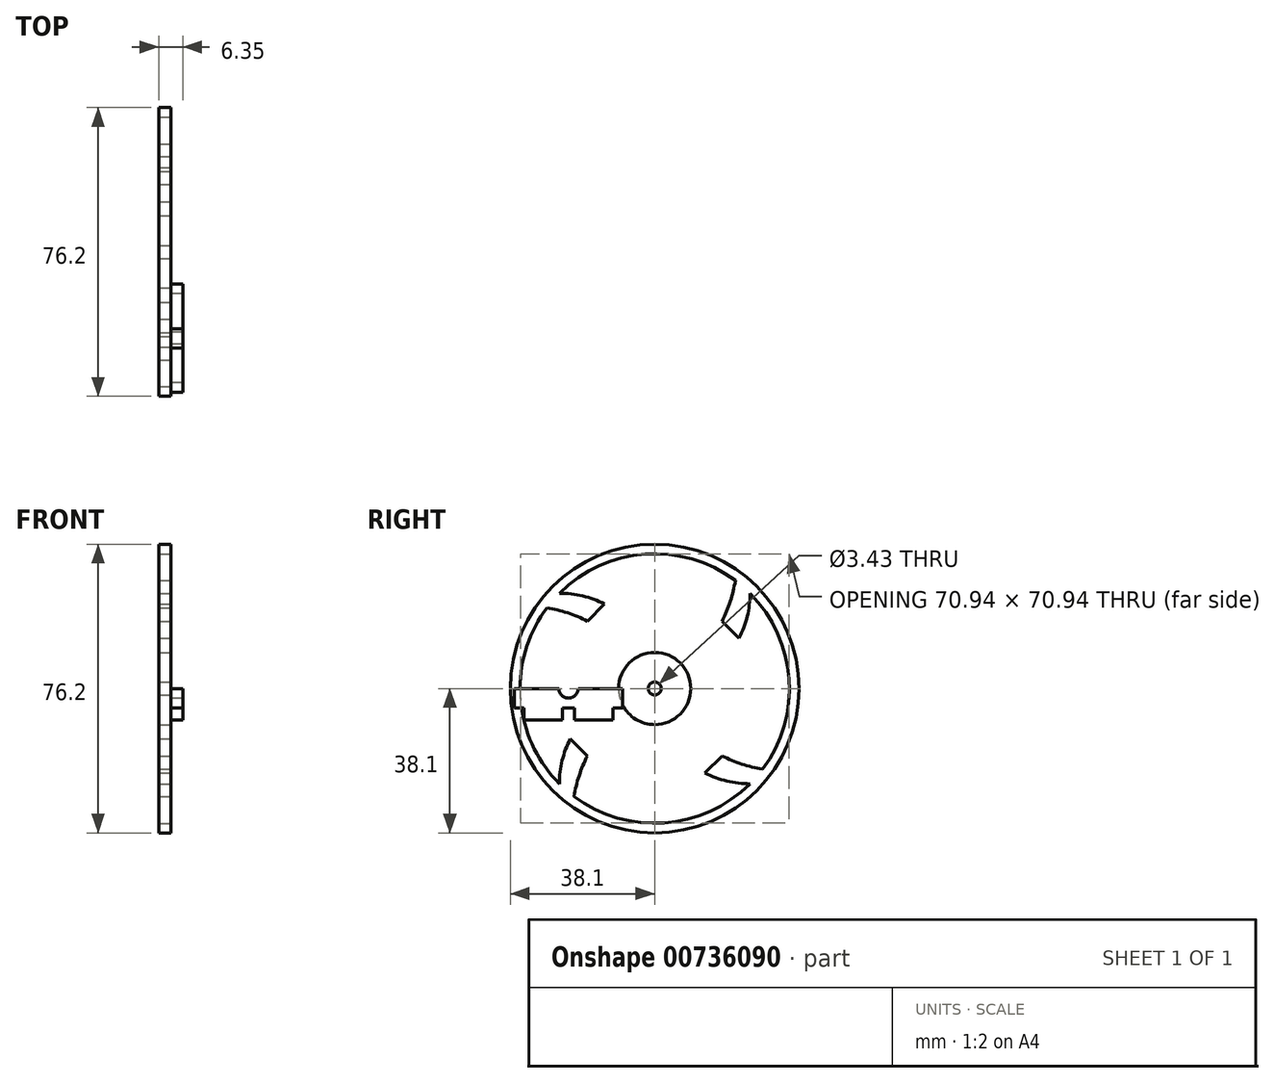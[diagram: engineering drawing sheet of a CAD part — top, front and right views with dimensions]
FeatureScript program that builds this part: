
annotation { "Feature Type Name" : "Feature", "Feature Type Description" : "" }
export const myFeature = defineFeature(function(context is Context, id is Id, definition is map)
    precondition{}
    {
        {
            var Q0;
            Q0=qCreatedBy(makeId("Right.planeOp"),FACE);
            var sketch = newSketch(context, id + "F0", { "sketchPlane" : qUnion([Q0])});
            skLineSegment(sketch, "E0.bottom", {"start": v(-34.5, -5.08) * mm, "end": v(-24.35, -5.08) * mm});
            skLineSegment(sketch, "E0.top", {"start": v(-34.5, -8.25) * mm, "end": v(-24.35, -8.25) * mm});
            skLineSegment(sketch, "E0.left", {"start": v(-34.5, -5.08) * mm, "end": v(-34.5, -8.25) * mm});
            skLineSegment(sketch, "E0.right", {"start": v(-24.35, -5.08) * mm, "end": v(-24.35, -8.25) * mm});
            skLineSegment(sketch, "E1", {"start": v(-24.35, -5.08) * mm, "end": v(-21.17, -5.08) * mm});
            skLineSegment(sketch, "E2.bottom", {"start": v(-21.17, -5.08) * mm, "end": v(-11.01, -5.08) * mm});
            skLineSegment(sketch, "E2.top", {"start": v(-21.17, -8.25) * mm, "end": v(-11.01, -8.25) * mm});
            skLineSegment(sketch, "E2.left", {"start": v(-21.17, -5.08) * mm, "end": v(-21.17, -8.25) * mm});
            skLineSegment(sketch, "E2.right", {"start": v(-11.01, -5.08) * mm, "end": v(-11.01, -8.25) * mm});
            skLineSegment(sketch, "E3", {"start": v(-11.01, -5.08) * mm, "end": v(-8.47, -5.08) * mm});
            skLineSegment(sketch, "E4", {"start": v(-8.47, -5.08) * mm, "end": v(-8.47, 0) * mm});
            skLineSegment(sketch, "E5", {"start": v(-34.5, -5.08) * mm, "end": v(-37.05, -5.08) * mm});
            skLineSegment(sketch, "E6", {"start": v(-37.05, -5.08) * mm, "end": v(-37.05, 0) * mm});
            skLineSegment(sketch, "E7", {"start": v(-37.05, 0) * mm, "end": v(-8.47, 0) * mm});
            skCircle(sketch, "E8", {"center": v(-22.76, 0) * mm, "radius": 1.59 * mm});
            skCircle(sketch, "E9", {"center": v(-22.76, 0) * mm, "radius": 2.54 * mm});
            skSolve(sketch);
        }
        {
            var Q0;
            Q0=makeQuery(id+"F0.imprint","IMPRINT",FACE,{"disambiguationData":[TD([[makeQuery(id+"F0.imprint","IMPRINT",EDGE,{"derivedFrom":sQuery(id+"F0.wireOp",EDGE,"E0.bottom")}),1.0]])]});
            var Q1;
            Q1=makeQuery(id+"F0.imprint","IMPRINT",FACE,{"disambiguationData":[TD([[makeQuery(id+"F0.imprint","IMPRINT",EDGE,{"derivedFrom":sQuery(id+"F0.wireOp",EDGE,"E0.bottom")}),-1.0]])]});
            var Q2;
            Q2=makeQuery(id+"F0.imprint","IMPRINT",FACE,{"disambiguationData":[TD([[makeQuery(id+"F0.imprint","IMPRINT",EDGE,{"derivedFrom":sQuery(id+"F0.wireOp",EDGE,"E2.bottom")}),-1.0]])]});
            var Q3;
            {var subQ0=sQuery(id+"F0.wireOp",EDGE,"E9");var subQ1=sQuery(id+"F0.wireOp",EDGE,"E7");var subQ2=makeQuery(id+"F0.imprint","INTERSECT",VERTEX,{"disambiguationData":[OD(0.0)],"derivedFrom":[subQ1,subQ0]});Q3=makeQuery(id+"F0.imprint","IMPRINT",FACE,{"disambiguationData":[TD([[makeQuery(id+"F0.imprint","IMPRINT",EDGE,{"disambiguationData":[TD([[subQ2,-1.0]])],"derivedFrom":subQ1}),-1.0]])]});}
            var Q4;
            {var subQ0=sQuery(id+"F0.wireOp",EDGE,"E9");var subQ1=sQuery(id+"F0.wireOp",EDGE,"E7");var subQ2=makeQuery(id+"F0.imprint","INTERSECT",VERTEX,{"disambiguationData":[OD(0.0)],"derivedFrom":[subQ1,subQ0]});Q4=makeQuery(id+"F0.imprint","IMPRINT",FACE,{"disambiguationData":[TD([[makeQuery(id+"F0.imprint","IMPRINT",EDGE,{"disambiguationData":[TD([[subQ2,-1.0]])],"derivedFrom":subQ1}),1.0]])]});}
            extrude(context, id + "F1", {"entities" : qUnion([Q0, Q1, Q2, Q3, Q4]), "depth" : 3.17 * mm, "offsetDistance" : 25.4 * mm});
        }
        {
            var Q0;
            Q0=qCreatedBy(makeId("Right.planeOp"),FACE);
            var sketch = newSketch(context, id + "F2", { "sketchPlane" : qUnion([Q0])});
            skCircle(sketch, "E10", {"center": v(0, 0) * mm, "radius": 1.71 * mm});
            skCircle(sketch, "E11", {"center": v(0, 0) * mm, "radius": 38.1 * mm});
            skCircle(sketch, "E12", {"center": v(0, 0) * mm, "radius": 35.56 * mm});
            skLineSegment(sketch, "E13", {"start": v(0, 35.56) * mm, "end": v(-35.56, 0) * mm});
            skLineSegment(sketch, "E14", {"start": v(-35.56, 0) * mm, "end": v(0, -35.56) * mm});
            skLineSegment(sketch, "E15", {"start": v(0, -35.56) * mm, "end": v(35.56, 0) * mm});
            skLineSegment(sketch, "E16", {"start": v(35.56, 0) * mm, "end": v(0, 35.56) * mm});
            skLineSegment(sketch, "E17", {"start": v(-17.78, 17.78) * mm, "end": v(-25.14, 25.14) * mm});
            skLineSegment(sketch, "E18", {"start": v(0, 0) * mm, "end": v(-1.21, -1.21) * mm});
            skLineSegment(sketch, "E19", {"start": v(0, 0) * mm, "end": v(-1.71, 0) * mm});
            skLineSegment(sketch, "E20", {"start": v(0, 0) * mm, "end": v(-1.21, 1.21) * mm});
            skLineSegment(sketch, "E21.MirrorCS", {"start": v(17.78, -17.78) * mm, "end": v(25.14, -25.14) * mm});
            skLineSegment(sketch, "E22", {"start": v(17.78, 17.78) * mm, "end": v(25.14, 25.14) * mm});
            skLineSegment(sketch, "E23.MirrorCS", {"start": v(-17.78, -17.78) * mm, "end": v(-25.14, -25.14) * mm});
            skLineSegment(sketch, "E24.MirrorCS", {"start": v(0, 0) * mm, "end": v(1.21, 1.21) * mm});
            skLineSegment(sketch, "E25.MirrorCS", {"start": v(0, 0) * mm, "end": v(1.21, -1.21) * mm});
            skLineSegment(sketch, "E26", {"start": v(0, 0) * mm, "end": v(0, 1.71) * mm});
            skLineSegment(sketch, "E27", {"start": v(0, 0) * mm, "end": v(1.71, 0) * mm});
            skLineSegment(sketch, "E28", {"start": v(0, 0) * mm, "end": v(0, -1.71) * mm});
            skLineSegment(sketch, "E29", {"start": v(-17.78, 17.78) * mm, "end": v(-13.29, 22.27) * mm});
            skLineSegment(sketch, "E30", {"start": v(17.78, 17.78) * mm, "end": v(22.27, 13.29) * mm});
            skLineSegment(sketch, "E31", {"start": v(-17.78, -17.78) * mm, "end": v(-22.27, -13.29) * mm});
            skLineSegment(sketch, "E32", {"start": v(17.78, -17.78) * mm, "end": v(13.29, -22.27) * mm});
            skLineSegment(sketch, "E33", {"start": v(-25.14, -25.14) * mm, "end": v(-21.3, -28.47) * mm});
            skLineSegment(sketch, "E34", {"start": v(25.14, -25.14) * mm, "end": v(28.47, -21.3) * mm});
            skLineSegment(sketch, "E35", {"start": v(25.14, 25.14) * mm, "end": v(21.3, 28.47) * mm});
            skLineSegment(sketch, "E36", {"start": v(-25.14, 25.14) * mm, "end": v(-28.47, 21.3) * mm});
            skArc(sketch, "E37", {"start": v(0, 1.71) * mm, "mid": v(-7.9, 18.44) * mm, "end": v(-25.14, 25.14) * mm});
            skArc(sketch, "E38", {"start": v(-1.21, 1.21) * mm, "mid": v(-12.45, 14.5) * mm, "end": v(-28.47, 21.3) * mm});
            skArc(sketch, "E39", {"start": v(-1.21, -1.21) * mm, "mid": v(-14.5, -12.45) * mm, "end": v(-21.3, -28.47) * mm});
            skArc(sketch, "E40", {"start": v(-1.71, 0) * mm, "mid": v(-18.44, -7.9) * mm, "end": v(-25.14, -25.14) * mm});
            skArc(sketch, "E41", {"start": v(0, -1.71) * mm, "mid": v(7.9, -18.44) * mm, "end": v(25.14, -25.14) * mm});
            skArc(sketch, "E42", {"start": v(1.21, -1.21) * mm, "mid": v(12.45, -14.5) * mm, "end": v(28.47, -21.3) * mm});
            skArc(sketch, "E43", {"start": v(1.71, 0) * mm, "mid": v(18.44, 7.9) * mm, "end": v(25.14, 25.14) * mm});
            skArc(sketch, "E44", {"start": v(1.21, 1.21) * mm, "mid": v(14.5, 12.45) * mm, "end": v(21.3, 28.47) * mm});
            skCircle(sketch, "E45", {"center": v(0, 0) * mm, "radius": 9.53 * mm});
            skSolve(sketch);
        }
        {
            var Q0;
            {var subQ5=sQuery(id+"F2.wireOp",EDGE,"E30");Q0=makeQuery(id+"F2.imprint","IMPRINT",FACE,{"disambiguationData":[TD([[makeQuery(id+"F2.imprint","IMPRINT",EDGE,{"derivedFrom":subQ5}),-1.0]])]});}
            var Q1;
            {var subQ0=sQuery(id+"F2.wireOp",EDGE,"E22");Q1=makeQuery(id+"F2.imprint","IMPRINT",FACE,{"disambiguationData":[TD([[makeQuery(id+"F2.imprint","IMPRINT",EDGE,{"derivedFrom":subQ0}),-1.0]])]});}
            var Q2;
            {var subQ0=sQuery(id+"F2.wireOp",EDGE,"E22");Q2=makeQuery(id+"F2.imprint","IMPRINT",FACE,{"disambiguationData":[TD([[makeQuery(id+"F2.imprint","IMPRINT",EDGE,{"derivedFrom":subQ0}),1.0]])]});}
            var Q3;
            Q3=makeQuery(id+"F2.imprint","IMPRINT",FACE,{"disambiguationData":[TD([[makeQuery(id+"F2.imprint","IMPRINT",EDGE,{"derivedFrom":sQuery(id+"F2.wireOp",EDGE,"E11")}),1.0]])]});
            var Q4;
            {var subQ5=sQuery(id+"F2.wireOp",EDGE,"E32");Q4=makeQuery(id+"F2.imprint","IMPRINT",FACE,{"disambiguationData":[TD([[makeQuery(id+"F2.imprint","IMPRINT",EDGE,{"derivedFrom":subQ5}),-1.0]])]});}
            var Q5;
            {var subQ0=sQuery(id+"F2.wireOp",EDGE,"E21.MirrorCS");Q5=makeQuery(id+"F2.imprint","IMPRINT",FACE,{"disambiguationData":[TD([[makeQuery(id+"F2.imprint","IMPRINT",EDGE,{"derivedFrom":subQ0}),-1.0]])]});}
            var Q6;
            {var subQ0=sQuery(id+"F2.wireOp",EDGE,"E21.MirrorCS");Q6=makeQuery(id+"F2.imprint","IMPRINT",FACE,{"disambiguationData":[TD([[makeQuery(id+"F2.imprint","IMPRINT",EDGE,{"derivedFrom":subQ0}),1.0]])]});}
            var Q7;
            {var subQ5=sQuery(id+"F2.wireOp",EDGE,"E31");Q7=makeQuery(id+"F2.imprint","IMPRINT",FACE,{"disambiguationData":[TD([[makeQuery(id+"F2.imprint","IMPRINT",EDGE,{"derivedFrom":subQ5}),-1.0]])]});}
            var Q8;
            {var subQ0=sQuery(id+"F2.wireOp",EDGE,"E23.MirrorCS");Q8=makeQuery(id+"F2.imprint","IMPRINT",FACE,{"disambiguationData":[TD([[makeQuery(id+"F2.imprint","IMPRINT",EDGE,{"derivedFrom":subQ0}),-1.0]])]});}
            var Q9;
            {var subQ0=sQuery(id+"F2.wireOp",EDGE,"E23.MirrorCS");Q9=makeQuery(id+"F2.imprint","IMPRINT",FACE,{"disambiguationData":[TD([[makeQuery(id+"F2.imprint","IMPRINT",EDGE,{"derivedFrom":subQ0}),1.0]])]});}
            var Q10;
            {var subQ5=sQuery(id+"F2.wireOp",EDGE,"E29");Q10=makeQuery(id+"F2.imprint","IMPRINT",FACE,{"disambiguationData":[TD([[makeQuery(id+"F2.imprint","IMPRINT",EDGE,{"derivedFrom":subQ5}),-1.0]])]});}
            var Q11;
            {var subQ0=sQuery(id+"F2.wireOp",EDGE,"E17");Q11=makeQuery(id+"F2.imprint","IMPRINT",FACE,{"disambiguationData":[TD([[makeQuery(id+"F2.imprint","IMPRINT",EDGE,{"derivedFrom":subQ0}),1.0]])]});}
            var Q12;
            {var subQ0=sQuery(id+"F2.wireOp",EDGE,"E17");Q12=makeQuery(id+"F2.imprint","IMPRINT",FACE,{"disambiguationData":[TD([[makeQuery(id+"F2.imprint","IMPRINT",EDGE,{"derivedFrom":subQ0}),-1.0]])]});}
            var Q13;
            {var subQ3=sQuery(id+"F2.wireOp",EDGE,"E38");var subQ5=sQuery(id+"F2.wireOp",EDGE,"E45");var subQ7=makeQuery(id+"F2.imprint","INTERSECT",VERTEX,{"derivedFrom":[subQ3,subQ5]});Q13=makeQuery(id+"F2.imprint","IMPRINT",FACE,{"disambiguationData":[TD([[makeQuery(id+"F2.imprint","IMPRINT",EDGE,{"disambiguationData":[TD([[subQ7,-1.0]])],"derivedFrom":subQ5}),1.0]])]});}
            var Q14;
            {var subQ3=sQuery(id+"F2.wireOp",EDGE,"E37");var subQ5=sQuery(id+"F2.wireOp",EDGE,"E45");var subQ7=makeQuery(id+"F2.imprint","INTERSECT",VERTEX,{"derivedFrom":[subQ3,subQ5]});Q14=makeQuery(id+"F2.imprint","IMPRINT",FACE,{"disambiguationData":[TD([[makeQuery(id+"F2.imprint","IMPRINT",EDGE,{"disambiguationData":[TD([[subQ7,-1.0]])],"derivedFrom":subQ5}),1.0]])]});}
            var Q15;
            {var subQ3=sQuery(id+"F2.wireOp",EDGE,"E37");var subQ5=sQuery(id+"F2.wireOp",EDGE,"E45");var subQ6=makeQuery(id+"F2.imprint","INTERSECT",VERTEX,{"derivedFrom":[subQ3,subQ5]});Q15=makeQuery(id+"F2.imprint","IMPRINT",FACE,{"disambiguationData":[TD([[makeQuery(id+"F2.imprint","IMPRINT",EDGE,{"disambiguationData":[TD([[subQ6,1.0]])],"derivedFrom":subQ5}),1.0]])]});}
            var Q16;
            {var subQ3=sQuery(id+"F2.wireOp",EDGE,"E43");var subQ5=sQuery(id+"F2.wireOp",EDGE,"E45");var subQ7=makeQuery(id+"F2.imprint","INTERSECT",VERTEX,{"derivedFrom":[subQ3,subQ5]});Q16=makeQuery(id+"F2.imprint","IMPRINT",FACE,{"disambiguationData":[TD([[makeQuery(id+"F2.imprint","IMPRINT",EDGE,{"disambiguationData":[TD([[subQ7,-1.0]])],"derivedFrom":subQ5}),1.0]])]});}
            var Q17;
            {var subQ0=sQuery(id+"F2.wireOp",EDGE,"E42");var subQ5=sQuery(id+"F2.wireOp",EDGE,"E45");var subQ7=makeQuery(id+"F2.imprint","INTERSECT",VERTEX,{"derivedFrom":[subQ0,subQ5]});Q17=makeQuery(id+"F2.imprint","IMPRINT",FACE,{"disambiguationData":[TD([[makeQuery(id+"F2.imprint","IMPRINT",EDGE,{"disambiguationData":[TD([[subQ7,-1.0]])],"derivedFrom":subQ5}),1.0]])]});}
            var Q18;
            {var subQ3=sQuery(id+"F2.wireOp",EDGE,"E41");var subQ5=sQuery(id+"F2.wireOp",EDGE,"E45");var subQ6=makeQuery(id+"F2.imprint","INTERSECT",VERTEX,{"derivedFrom":[subQ3,subQ5]});Q18=makeQuery(id+"F2.imprint","IMPRINT",FACE,{"disambiguationData":[TD([[makeQuery(id+"F2.imprint","IMPRINT",EDGE,{"disambiguationData":[TD([[subQ6,-1.0]])],"derivedFrom":subQ5}),1.0]])]});}
            var Q19;
            {var subQ0=sQuery(id+"F2.wireOp",EDGE,"E39");var subQ5=sQuery(id+"F2.wireOp",EDGE,"E45");var subQ6=makeQuery(id+"F2.imprint","INTERSECT",VERTEX,{"derivedFrom":[subQ0,subQ5]});Q19=makeQuery(id+"F2.imprint","IMPRINT",FACE,{"disambiguationData":[TD([[makeQuery(id+"F2.imprint","IMPRINT",EDGE,{"disambiguationData":[TD([[subQ6,1.0]])],"derivedFrom":subQ5}),1.0]])]});}
            var Q20;
            {var subQ0=sQuery(id+"F2.wireOp",EDGE,"E39");var subQ5=sQuery(id+"F2.wireOp",EDGE,"E45");var subQ6=makeQuery(id+"F2.imprint","INTERSECT",VERTEX,{"derivedFrom":[subQ0,subQ5]});Q20=makeQuery(id+"F2.imprint","IMPRINT",FACE,{"disambiguationData":[TD([[makeQuery(id+"F2.imprint","IMPRINT",EDGE,{"disambiguationData":[TD([[subQ6,-1.0]])],"derivedFrom":subQ5}),1.0]])]});}
            var Q21;
            {var subQ0=sQuery(id+"F2.wireOp",EDGE,"E36");Q21=makeQuery(id+"F2.imprint","IMPRINT",FACE,{"disambiguationData":[TD([[makeQuery(id+"F2.imprint","IMPRINT",EDGE,{"derivedFrom":subQ0}),-1.0]])]});}
            var Q22;
            {var subQ0=sQuery(id+"F2.wireOp",EDGE,"E35");Q22=makeQuery(id+"F2.imprint","IMPRINT",FACE,{"disambiguationData":[TD([[makeQuery(id+"F2.imprint","IMPRINT",EDGE,{"derivedFrom":subQ0}),-1.0]])]});}
            var Q23;
            {var subQ0=sQuery(id+"F2.wireOp",EDGE,"E34");Q23=makeQuery(id+"F2.imprint","IMPRINT",FACE,{"disambiguationData":[TD([[makeQuery(id+"F2.imprint","IMPRINT",EDGE,{"derivedFrom":subQ0}),-1.0]])]});}
            var Q24;
            {var subQ0=sQuery(id+"F2.wireOp",EDGE,"E33");Q24=makeQuery(id+"F2.imprint","IMPRINT",FACE,{"disambiguationData":[TD([[makeQuery(id+"F2.imprint","IMPRINT",EDGE,{"derivedFrom":subQ0}),-1.0]])]});}
            extrude(context, id + "F3", {"entities" : qUnion([Q0, Q1, Q2, Q3, Q4, Q5, Q6, Q7, Q8, Q9, Q10, Q11, Q12, Q13, Q14, Q15, Q16, Q17, Q18, Q19, Q20, Q21, Q22, Q23, Q24]), "oppositeDirection" : true, "depth" : 3.17 * mm, "offsetDistance" : 25.4 * mm});
        }
    });
